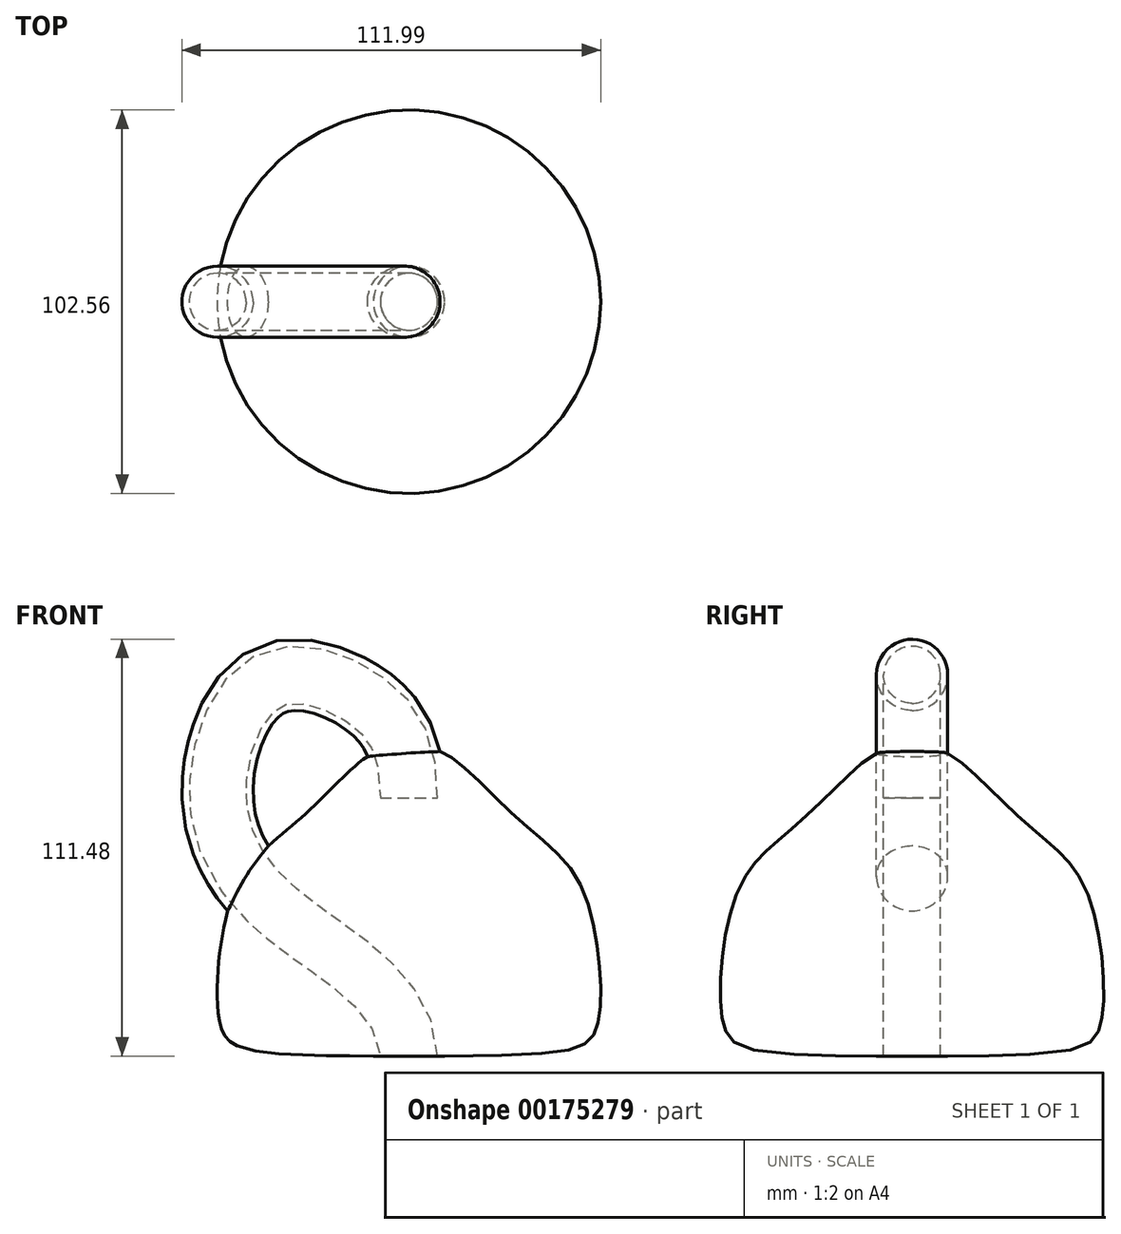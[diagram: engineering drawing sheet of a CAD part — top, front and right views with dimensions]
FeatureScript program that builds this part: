
annotation { "Feature Type Name" : "Feature", "Feature Type Description" : "" }
export const myFeature = defineFeature(function(context is Context, id is Id, definition is map)
    precondition{}
    {
        {
            var Q0;
            Q0=qCreatedBy(makeId("Front.planeOp"),FACE);
            var sketch = newSketch(context, id + "F0", { "sketchPlane" : qUnion([Q0])});
            skLineSegment(sketch, "E0", {"start": v(0, 0) * mm, "end": v(91.36, 0) * mm, "construction": true});
            skFitSpline(sketch, "E1", {"points": [v(0, 0) * mm, v(50.3, 7.93) * mm, v(50.73, 26.4) * mm, v(44.26, 48.63) * mm, v(28.67, 63.9) * mm, v(11.95, 79.5) * mm, v(0, 81.93) * mm], "startDerivative": vector(518.7, 0) * mm, "endDerivative": vector(-156.27, -11) * mm});
            skLineSegment(sketch, "E2", {"start": v(0, 81.93) * mm, "end": v(0, 0) * mm});
            skSolve(sketch);
        }
        {
            var Q0;
            Q0=qCreatedBy(makeId("Front.planeOp"),FACE);
            var sketch = newSketch(context, id + "F1", { "sketchPlane" : qUnion([Q0])});
            skFitSpline(sketch, "E3", {"points": [v(0, 69.02) * mm, v(-11.16, 94.93) * mm, v(-37.67, 100.31) * mm, v(-51.17, 69.53) * mm, v(-38.58, 42.16) * mm, v(-13.45, 22.6) * mm, v(0, 0) * mm], "startDerivative": vector(0, 245.32) * mm, "endDerivative": vector(0, -171.68) * mm});
            skSolve(sketch);
        }
        {
            var Q0;
            Q0=qCreatedBy(makeId("Top.planeOp"),FACE);
            var sketch = newSketch(context, id + "F2", { "sketchPlane" : qUnion([Q0])});
            skCircle(sketch, "E4", {"center": v(0, 0) * mm, "radius": 9.53 * mm});
            skSolve(sketch);
        }
        {
            var Q0;
            Q0=qCreatedBy(makeId("Top.planeOp"),FACE);
            var sketch = newSketch(context, id + "F3", { "sketchPlane" : qUnion([Q0])});
            skCircle(sketch, "E5", {"center": v(0, 0) * mm, "radius": 7.62 * mm});
            skSolve(sketch);
        }
        {
            var Q0;
            Q0=makeQuery(id+"F0.imprint","IMPRINT",FACE,{"disambiguationData":[TD([[makeQuery(id+"F0.imprint","IMPRINT",EDGE,{"derivedFrom":sQuery(id+"F0.wireOp",EDGE,"E1")}),1.0]])]});
            var Q1;
            Q1=sQuery(id+"F0.wireOp",EDGE,"E2");
            revolve(context, id + "F4", {"entities" : qUnion([Q0]), "axis" : qUnion([Q1]), "revolveType" : RevolveType.FULL});
        }
        {
            var Q0;
            Q0 = qSketchRegion(id + "F2", true);
            var Q1;
            Q1 = qConstructionFilter(qBodyType(qCreatedBy(id + "F1" ,EDGE), BodyType.WIRE), ConstructionObject.NO);
            sweep(context, id + "F5", {"operationType" : NewBodyOperationType.ADD, "profiles" : qUnion([Q0]), "path" : qUnion([Q1])});
        }
        {
            var Q0;
            Q0 = qSketchRegion(id + "F3", true);
            var Q1;
            Q1 = qConstructionFilter(qBodyType(qCreatedBy(id + "F1" ,EDGE), BodyType.WIRE), ConstructionObject.NO);
            sweep(context, id + "F6", {"operationType" : NewBodyOperationType.REMOVE, "profiles" : qUnion([Q0]), "path" : qUnion([Q1])});
        }
    });
